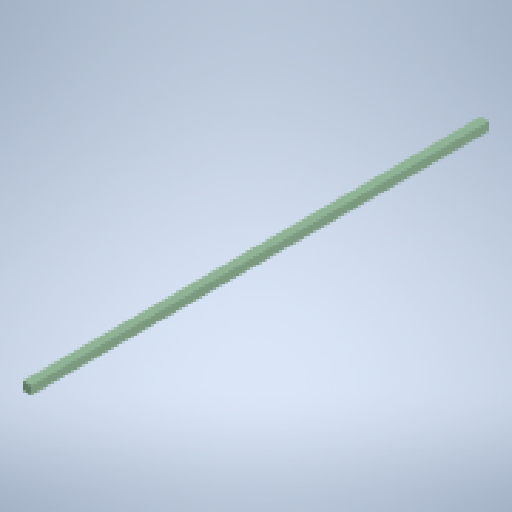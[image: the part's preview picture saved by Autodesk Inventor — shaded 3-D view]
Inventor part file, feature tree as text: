
AUTODESK INVENTOR PART (.ipt)
format: ipt  version: 2025.1 (Build 291241020, 241B)  size: 139,264 bytes
history: native  units: in
note: dims shown in document units (in); Inventor stores cm internally (conversion verified against a paired STEP export)
features: other x2, extrude x1, sketch x1
ambient origin geometry x8: Origin, YZ Plane, XZ Plane, XY Plane, X Axis, Y Axis, Z Axis, Center Point
bodies: Solid1 (feature_tree)
feature tree (4):
  extrude  "Extrusion1"  Depth=3.5in
  sketch  "Sketch1"  dims[d0=3.5in d1=3.5in d2=192.0in d3=0.0in]
  other  "Finish1"
  other  "Finish2"
